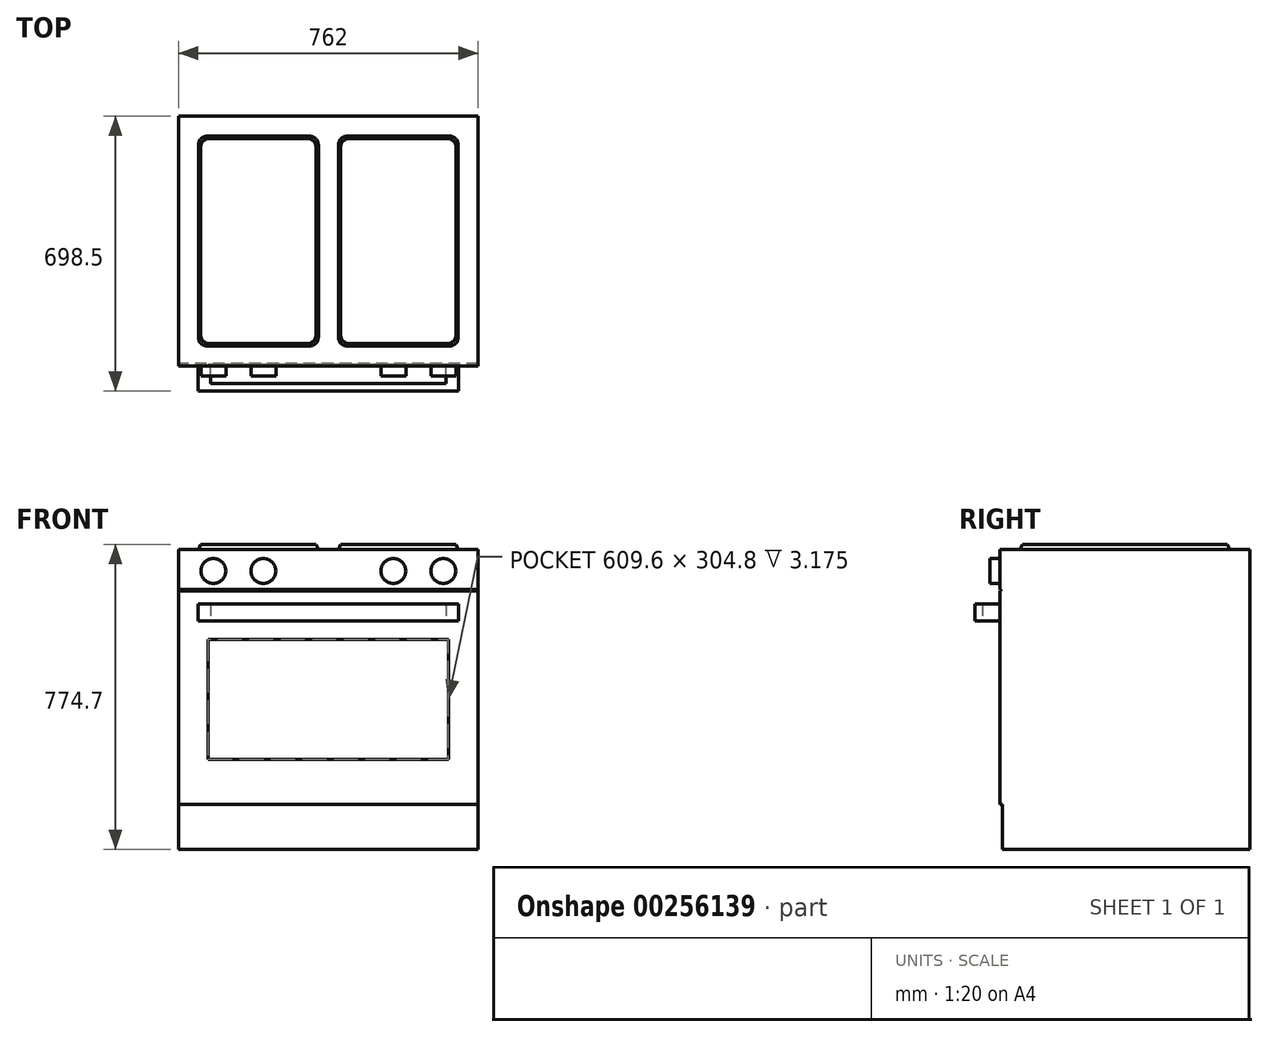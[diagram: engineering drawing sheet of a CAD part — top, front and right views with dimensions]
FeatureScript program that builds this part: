
annotation { "Feature Type Name" : "Feature", "Feature Type Description" : "" }
export const myFeature = defineFeature(function(context is Context, id is Id, definition is map)
    precondition{}
    {
        {
            var Q0;
            Q0=qCreatedBy(makeId("Right.planeOp"),FACE);
            var sketch = newSketch(context, id + "F0", { "sketchPlane" : qUnion([Q0])});
            skLineSegment(sketch, "E0", {"start": v(0, 0) * mm, "end": v(0, 762) * mm});
            skLineSegment(sketch, "E1", {"start": v(0, 0) * mm, "end": v(-628.65, 0) * mm});
            skLineSegment(sketch, "E2", {"start": v(-628.65, 0) * mm, "end": v(-628.65, 113.82) * mm});
            skLineSegment(sketch, "E3", {"start": v(-628.65, 113.82) * mm, "end": v(-635, 113.82) * mm});
            skLineSegment(sketch, "E4", {"start": v(-635, 113.82) * mm, "end": v(-635, 657.23) * mm});
            skLineSegment(sketch, "E5", {"start": v(-635, 657.23) * mm, "end": v(-631.82, 657.23) * mm});
            skLineSegment(sketch, "E6", {"start": v(-631.82, 657.23) * mm, "end": v(-631.82, 660.4) * mm});
            skLineSegment(sketch, "E7", {"start": v(-631.82, 660.4) * mm, "end": v(-635, 660.4) * mm});
            skLineSegment(sketch, "E8", {"start": v(-635, 660.4) * mm, "end": v(-635, 762) * mm});
            skLineSegment(sketch, "E9", {"start": v(-635, 762) * mm, "end": v(0, 762) * mm});
            skSolve(sketch);
        }
        {
            var Q0;
            Q0=makeQuery(id+"F0.imprint","IMPRINT",FACE,{"disambiguationData":[TD([[makeQuery(id+"F0.imprint","IMPRINT",EDGE,{"derivedFrom":sQuery(id+"F0.wireOp",EDGE,"E0")}),1.0]])]});
            extrude(context, id + "F1", {"entities" : qUnion([Q0]), "endBound" : BoundingType.SYMMETRIC, "depth" : 762 * mm});
        }
        {
            var Q0;
            Q0=makeQuery(id+"F1.opExtrude","SWEPT_FACE",FACE,{"disambiguationData":[OSD([sQuery(id+"F0.wireOp",EDGE,"E4")])]});
            var sketch = newSketch(context, id + "F2", { "sketchPlane" : qUnion([Q0])});
            skLineSegment(sketch, "E10.bottom", {"start": v(304.8, 228.6) * mm, "end": v(-304.8, 228.6) * mm});
            skLineSegment(sketch, "E10.top", {"start": v(304.8, 533.4) * mm, "end": v(-304.8, 533.4) * mm});
            skLineSegment(sketch, "E10.left", {"start": v(304.8, 228.6) * mm, "end": v(304.8, 533.4) * mm});
            skLineSegment(sketch, "E10.right", {"start": v(-304.8, 228.6) * mm, "end": v(-304.8, 533.4) * mm});
            skPoint(sketch, "E10.middle", {"position": v(0, 381) * mm});
            skSolve(sketch);
        }
        {
            var Q0;
            Q0 = qSketchRegion(id + "F2", true);
            extrude(context, id + "F3", {"entities" : qUnion([Q0]), "operationType" : NewBodyOperationType.REMOVE, "oppositeDirection" : true, "depth" : 3.17 * mm});
        }
        {
            var Q0;
            Q0=qCreatedBy(makeId("Top.planeOp"),FACE);
            cPlane(context, id + "F4", {"entities" : qUnion([Q0]), "cplaneType" : CPlaneType.OFFSET, "offset" : 601.98 * mm, "width" : 152.4 * mm, "height" : 152.4 * mm});
        }
        {
            var Q0;
            Q0=qCreatedBy(id+"F4.planeOp",FACE);
            var sketch = newSketch(context, id + "F5", { "sketchPlane" : qUnion([Q0])});
            skLineSegment(sketch, "E11.bottom", {"start": v(330.35, -698.5) * mm, "end": v(-330.35, -698.5) * mm});
            skPoint(sketch, "E11.middle", {"position": v(0, -688.98) * mm});
            skLineSegment(sketch, "E12.top", {"start": v(-330.35, -609.34) * mm, "end": v(-298.6, -609.34) * mm});
            skLineSegment(sketch, "E12.left", {"start": v(-330.35, -698.5) * mm, "end": v(-330.35, -609.34) * mm});
            skLineSegment(sketch, "E12.right", {"start": v(-298.6, -679.45) * mm, "end": v(-298.6, -609.34) * mm});
            skLineSegment(sketch, "E13.MirrorCS", {"start": v(330.35, -698.5) * mm, "end": v(330.35, -609.34) * mm});
            skLineSegment(sketch, "E14.MirrorCS", {"start": v(298.6, -679.45) * mm, "end": v(298.6, -609.34) * mm});
            skLineSegment(sketch, "E15.MirrorCS", {"start": v(330.35, -609.34) * mm, "end": v(298.6, -609.34) * mm});
            skLineSegment(sketch, "E16", {"start": v(-298.6, -679.45) * mm, "end": v(298.6, -679.45) * mm});
            skSolve(sketch);
        }
        {
            var Q0;
            Q0 = qSketchRegion(id + "F5", true);
            extrude(context, id + "F6", {"entities" : qUnion([Q0]), "operationType" : NewBodyOperationType.ADD, "endBound" : BoundingType.SYMMETRIC, "depth" : 43.18 * mm});
        }
        {
            var Q0;
            Q0=makeQuery(id+"F1.opExtrude","SWEPT_FACE",FACE,{"disambiguationData":[OSD([sQuery(id+"F0.wireOp",EDGE,"E8")])]});
            var sketch = newSketch(context, id + "F7", { "sketchPlane" : qUnion([Q0])});
            skCircle(sketch, "E17", {"center": v(-292.1, 707.48) * mm, "radius": 31.75 * mm});
            skCircle(sketch, "E18", {"center": v(-165.1, 707.48) * mm, "radius": 31.75 * mm});
            skCircle(sketch, "E19.MirrorC", {"center": v(165.1, 707.48) * mm, "radius": 31.75 * mm});
            skCircle(sketch, "E20.MirrorC", {"center": v(292.1, 707.48) * mm, "radius": 31.75 * mm});
            skSolve(sketch);
        }
        {
            var Q0;
            Q0 = qSketchRegion(id + "F7", true);
            extrude(context, id + "F8", {"entities" : qUnion([Q0]), "operationType" : NewBodyOperationType.ADD, "depth" : 25.4 * mm});
        }
        {
            var Q0;
            Q0=makeQuery(id+"F1.opExtrude","SWEPT_FACE",FACE,{"disambiguationData":[OSD([sQuery(id+"F0.wireOp",EDGE,"E9")])]});
            var sketch = newSketch(context, id + "F9", { "sketchPlane" : qUnion([Q0])});
            skLineSegment(sketch, "E21.bottom", {"start": v(-330.2, -50.8) * mm, "end": v(-25.4, -50.8) * mm});
            skLineSegment(sketch, "E21.top", {"start": v(-330.2, -584.2) * mm, "end": v(-25.4, -584.2) * mm});
            skLineSegment(sketch, "E21.left", {"start": v(-330.2, -50.8) * mm, "end": v(-330.2, -584.2) * mm});
            skLineSegment(sketch, "E21.right", {"start": v(-25.4, -50.8) * mm, "end": v(-25.4, -584.2) * mm});
            skLineSegment(sketch, "E22.MirrorCS", {"start": v(25.4, -50.8) * mm, "end": v(25.4, -584.2) * mm});
            skLineSegment(sketch, "E23.MirrorCS", {"start": v(330.2, -50.8) * mm, "end": v(330.2, -584.2) * mm});
            skLineSegment(sketch, "E24.MirrorCS", {"start": v(330.2, -584.2) * mm, "end": v(25.4, -584.2) * mm});
            skLineSegment(sketch, "E25.MirrorCS", {"start": v(330.2, -50.8) * mm, "end": v(25.4, -50.8) * mm});
            skSolve(sketch);
        }
        {
            var Q0;
            Q0 = qSketchRegion(id + "F9", true);
            extrude(context, id + "F10", {"entities" : qUnion([Q0]), "operationType" : NewBodyOperationType.ADD, "depth" : 12.7 * mm, "hasDraft" : true, "draftAngle" : 25 * degree, "draftPullDirection" : true});
        }
        {
            var Q0;
            Q0=makeQuery(id+"F10.opExtrude","SWEPT_EDGE",EDGE,{"disambiguationData":[OSD([sQuery(id+"F9.wireOp",EDGE,"E21.top"),sQuery(id+"F9.wireOp",EDGE,"E21.left")])]});
            var Q1;
            Q1=makeQuery(id+"F10.opExtrude","SWEPT_EDGE",EDGE,{"disambiguationData":[OSD([sQuery(id+"F9.wireOp",EDGE,"E21.top"),sQuery(id+"F9.wireOp",EDGE,"E21.right")])]});
            var Q2;
            Q2=makeQuery(id+"F10.opExtrude","SWEPT_EDGE",EDGE,{"disambiguationData":[OSD([sQuery(id+"F9.wireOp",EDGE,"E22.MirrorCS"),sQuery(id+"F9.wireOp",EDGE,"E24.MirrorCS")])]});
            var Q3;
            Q3=makeQuery(id+"F10.opExtrude","SWEPT_EDGE",EDGE,{"disambiguationData":[OSD([sQuery(id+"F9.wireOp",EDGE,"E22.MirrorCS"),sQuery(id+"F9.wireOp",EDGE,"E25.MirrorCS")])]});
            var Q4;
            Q4=makeQuery(id+"F10.opExtrude","SWEPT_EDGE",EDGE,{"disambiguationData":[OSD([sQuery(id+"F9.wireOp",EDGE,"E21.bottom"),sQuery(id+"F9.wireOp",EDGE,"E21.left")])]});
            var Q5;
            Q5=makeQuery(id+"F10.opExtrude","SWEPT_EDGE",EDGE,{"disambiguationData":[OSD([sQuery(id+"F9.wireOp",EDGE,"E23.MirrorCS"),sQuery(id+"F9.wireOp",EDGE,"E24.MirrorCS")])]});
            var Q6;
            Q6=makeQuery(id+"F10.opExtrude","SWEPT_EDGE",EDGE,{"disambiguationData":[OSD([sQuery(id+"F9.wireOp",EDGE,"E23.MirrorCS"),sQuery(id+"F9.wireOp",EDGE,"E25.MirrorCS")])]});
            var Q7;
            Q7=makeQuery(id+"F10.opExtrude","SWEPT_EDGE",EDGE,{"disambiguationData":[OSD([sQuery(id+"F9.wireOp",EDGE,"E21.bottom"),sQuery(id+"F9.wireOp",EDGE,"E21.right")])]});
            fillet(context, id + "F11", {"entities" : qUnion([Q0, Q1, Q2, Q3, Q4, Q5, Q6, Q7]), "radius" : 25.4 * mm, "tangentPropagation" : true, "allowEdgeOverflow" : false});
        }
    });
